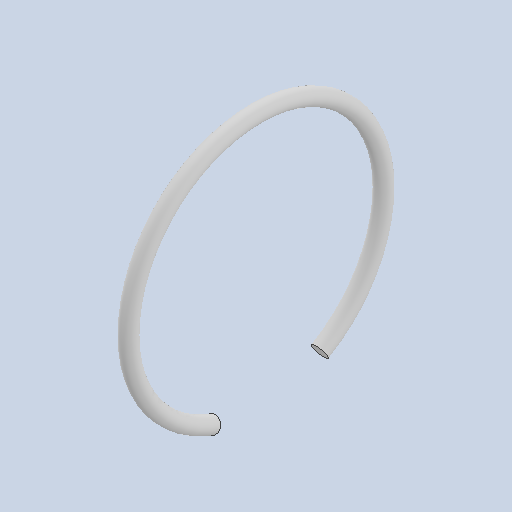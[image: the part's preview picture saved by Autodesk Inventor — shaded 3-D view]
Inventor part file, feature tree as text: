
AUTODESK INVENTOR PART (.ipt)
format: ipt  version: 2025.2 (Build 292293000, 293)  size: 103,936 bytes
history: native  units: in
note: dims shown in document units (in); Inventor stores cm internally (conversion verified against a paired STEP export)
features: revolve x1
ambient origin geometry x8: Origin, YZ Plane, XZ Plane, XY Plane, X Axis, Y Axis, Z Axis, Center Point
bodies: Solid1 (feature_tree)
feature tree (1):
  revolve  "Revolve1"  [1 undecoded]
note: 1 required parameter value undecoded (feature->parameter linkage not recoverable at this tier; creation-order binding heuristic only, values carry confidence <= 0.55)
